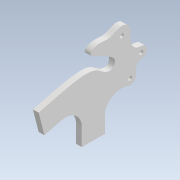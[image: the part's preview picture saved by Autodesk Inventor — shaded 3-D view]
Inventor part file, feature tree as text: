
AUTODESK INVENTOR PART (.ipt)
format: ipt  version: 2021 (Build 250183000, 183)  size: 154,112 bytes
history: native  units: mm
features: sketch x3, hole x2, other x1, extrude x1
ambient origin geometry x8: Origin, YZ Plane, XZ Plane, XY Plane, X Axis, Y Axis, Z Axis, Center Point
bodies: Body1 (feature_tree)
feature tree (7):
  other  "Sólido1"
  extrude  "Extrusión1"  Depth=10.0mm TaperAngle=0.0deg
  hole  "Agujero1"  [1 undecoded]
  hole  "Agujero2"  [1 undecoded]
  sketch  "Boceto1"  dims[d0=20.0mm d1=6.981317mm d2=15.0mm d3=9.526623mm d4=15.0mm d5=10.0mm d6=10.0mm d7=60.109139mm d8=50.0mm d9=5.0mm d10=0.0mm]
  sketch  "Boceto2"  dims[d11=3.4mm d12=6.0mm d13=6.3mm d14=2.0mm d15=90.0deg d16=8.0mm d17=20.594885mm]
  sketch  "Boceto3"  dims[d18=3.4mm d19=6.0mm d20=6.3mm d21=2.0mm d22=90.0deg d23=8.0mm d24=20.594885mm]
note: 2 required parameter values undecoded (feature->parameter linkage not recoverable at this tier; creation-order binding heuristic only, values carry confidence <= 0.55)
